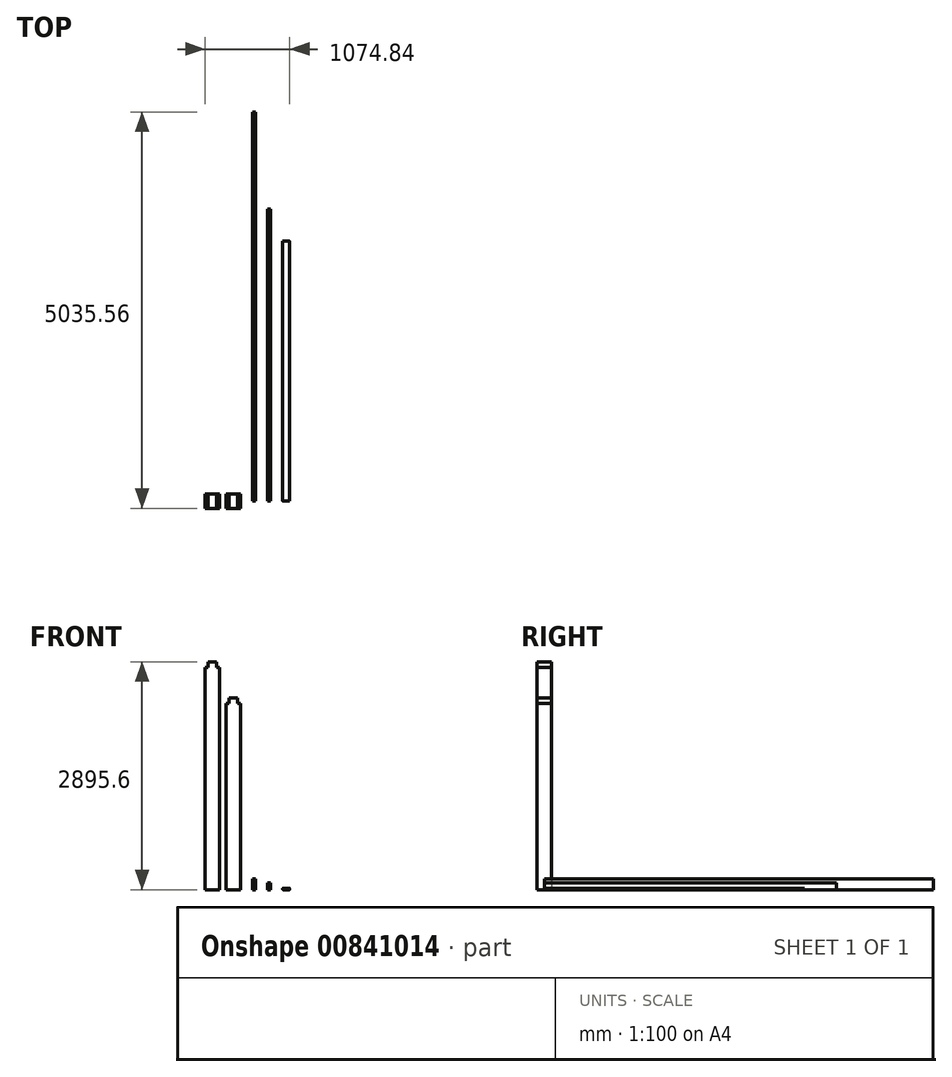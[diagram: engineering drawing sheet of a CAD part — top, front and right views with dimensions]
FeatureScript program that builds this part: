
annotation { "Feature Type Name" : "Feature", "Feature Type Description" : "" }
export const myFeature = defineFeature(function(context is Context, id is Id, definition is map)
    precondition{}
    {
        {
            var Q0;
            Q0=qCreatedBy(makeId("Top.planeOp"),FACE);
            var sketch = newSketch(context, id + "F0", { "sketchPlane" : qUnion([Q0])});
            skLineSegment(sketch, "E0.bottom", {"start": v(92.07, -92.08) * mm, "end": v(-92.08, -92.07) * mm});
            skLineSegment(sketch, "E0.top", {"start": v(92.07, 92.07) * mm, "end": v(-92.08, 92.08) * mm});
            skLineSegment(sketch, "E0.left", {"start": v(92.07, -92.08) * mm, "end": v(92.08, 92.08) * mm});
            skLineSegment(sketch, "E0.right", {"start": v(-92.08, -92.07) * mm, "end": v(-92.07, 92.07) * mm});
            skPoint(sketch, "E0.middle", {"position": v(0, 0) * mm});
            skLineSegment(sketch, "E1.bottom", {"start": v(360.46, -92.08) * mm, "end": v(176.31, -92.08) * mm});
            skLineSegment(sketch, "E1.top", {"start": v(360.46, 92.08) * mm, "end": v(176.31, 92.08) * mm});
            skLineSegment(sketch, "E1.left", {"start": v(360.46, -92.08) * mm, "end": v(360.46, 92.07) * mm});
            skLineSegment(sketch, "E1.right", {"start": v(176.31, -92.08) * mm, "end": v(176.31, 92.08) * mm});
            skPoint(sketch, "E1.middle", {"position": v(268.39, 0) * mm});
            skPoint(sketch, "E1.middle.positionSnap0", {"position": v(92.08, 0) * mm});
            skPoint(sketch, "E1.centerSnap0", {"position": v(92.08, 0) * mm});
            skSolve(sketch);
        }
        {
            var Q0;
            Q0=makeQuery(id+"F0.imprint","IMPRINT",FACE,{"disambiguationData":[TD([[makeQuery(id+"F0.imprint","IMPRINT",EDGE,{"derivedFrom":sQuery(id+"F0.wireOp",EDGE,"E0.bottom")}),-1.0]])]});
            extrude(context, id + "F1", {"entities" : qUnion([Q0]), "depth" : 2895.6 * mm, "offsetDistance" : 25.4 * mm});
        }
        {
            var Q0;
            Q0=makeQuery(id+"F0.imprint","IMPRINT",FACE,{"disambiguationData":[TD([[makeQuery(id+"F0.imprint","IMPRINT",EDGE,{"derivedFrom":sQuery(id+"F0.wireOp",EDGE,"E1.bottom")}),-1.0]])]});
            extrude(context, id + "F2", {"entities" : qUnion([Q0]), "depth" : 2438.4 * mm, "offsetDistance" : 25.4 * mm});
        }
        {
            var Q0;
            Q0=qCreatedBy(makeId("Front.planeOp"),FACE);
            var sketch = newSketch(context, id + "F3", { "sketchPlane" : qUnion([Q0])});
            skLineSegment(sketch, "E2.bottom", {"start": v(512.86, 0) * mm, "end": v(550.96, 0) * mm});
            skLineSegment(sketch, "E2.top", {"start": v(512.86, 139.7) * mm, "end": v(550.96, 139.7) * mm});
            skLineSegment(sketch, "E2.left", {"start": v(512.86, 0) * mm, "end": v(512.86, 139.7) * mm});
            skLineSegment(sketch, "E2.right", {"start": v(550.96, 0) * mm, "end": v(550.96, 139.7) * mm});
            skSolve(sketch);
        }
        {
            var Q0;
            Q0=makeQuery(id+"F3.imprint","IMPRINT",FACE,{"disambiguationData":[TD([[makeQuery(id+"F3.imprint","IMPRINT",EDGE,{"derivedFrom":sQuery(id+"F3.wireOp",EDGE,"E2.bottom")}),1.0]])]});
            extrude(context, id + "F4", {"entities" : qUnion([Q0]), "oppositeDirection" : true, "depth" : 4943.47 * mm, "offsetDistance" : 25.4 * mm});
        }
        {
            var Q0;
            Q0=makeQuery(id+"F2.opExtrude","SWEPT_FACE",FACE,{"disambiguationData":[OSD([sQuery(id+"F0.wireOp",EDGE,"E1.bottom")])]});
            var sketch = newSketch(context, id + "F5", { "sketchPlane" : qUnion([Q0])});
            skLineSegment(sketch, "E3.bottom", {"start": v(360.46, 2438.4) * mm, "end": v(322.36, 2438.4) * mm});
            skLineSegment(sketch, "E3.top", {"start": v(360.46, 2368.55) * mm, "end": v(322.36, 2368.55) * mm});
            skLineSegment(sketch, "E3.left", {"start": v(360.46, 2438.4) * mm, "end": v(360.46, 2368.55) * mm});
            skLineSegment(sketch, "E3.right", {"start": v(322.36, 2438.4) * mm, "end": v(322.36, 2368.55) * mm});
            skLineSegment(sketch, "E4", {"start": v(268.39, 2438.4) * mm, "end": v(268.39, 2178.62) * mm});
            skLineSegment(sketch, "E5.MirrorCS", {"start": v(214.41, 2438.4) * mm, "end": v(214.41, 2368.55) * mm});
            skLineSegment(sketch, "E6.MirrorCS", {"start": v(176.31, 2438.4) * mm, "end": v(214.41, 2438.4) * mm});
            skLineSegment(sketch, "E7.MirrorCS", {"start": v(176.31, 2368.55) * mm, "end": v(214.41, 2368.55) * mm});
            skLineSegment(sketch, "E8.MirrorCS", {"start": v(176.31, 2438.4) * mm, "end": v(176.31, 2368.55) * mm});
            skSolve(sketch);
        }
        {
            var Q0;
            Q0 = qSketchRegion(id + "F5", true);
            var Q1;
            Q1=makeQuery(id+"F2.opExtrude","SWEPT_FACE",FACE,{"disambiguationData":[OSD([sQuery(id+"F0.wireOp",EDGE,"E1.top")])]});
            extrude(context, id + "F6", {"entities" : qUnion([Q0]), "operationType" : NewBodyOperationType.REMOVE, "endBound" : BoundingType.UP_TO_SURFACE, "oppositeDirection" : true, "depth" : 25.4 * mm, "endBoundEntityFace" : qUnion([Q1]), "offsetDistance" : 25.4 * mm});
        }
        {
            var Q0;
            Q0=makeQuery(id+"F1.opExtrude","SWEPT_FACE",FACE,{"disambiguationData":[OSD([sQuery(id+"F0.wireOp",EDGE,"E0.bottom")])]});
            var sketch = newSketch(context, id + "F7", { "sketchPlane" : qUnion([Q0])});
            skLineSegment(sketch, "E9", {"start": v(0, 2895.6) * mm, "end": v(0, 2754.1) * mm});
            skLineSegment(sketch, "E10.bottom", {"start": v(-92.08, 2895.6) * mm, "end": v(-53.98, 2895.6) * mm});
            skLineSegment(sketch, "E10.top", {"start": v(-92.08, 2825.75) * mm, "end": v(-53.98, 2825.75) * mm});
            skLineSegment(sketch, "E10.left", {"start": v(-92.08, 2895.6) * mm, "end": v(-92.08, 2825.75) * mm});
            skLineSegment(sketch, "E10.right", {"start": v(-53.98, 2895.6) * mm, "end": v(-53.98, 2825.75) * mm});
            skLineSegment(sketch, "E11.MirrorCS", {"start": v(92.08, 2895.6) * mm, "end": v(92.08, 2825.75) * mm});
            skLineSegment(sketch, "E12.MirrorCS", {"start": v(92.08, 2825.75) * mm, "end": v(53.98, 2825.75) * mm});
            skLineSegment(sketch, "E13.MirrorCS", {"start": v(92.08, 2895.6) * mm, "end": v(53.98, 2895.6) * mm});
            skLineSegment(sketch, "E14.MirrorCS", {"start": v(53.98, 2895.6) * mm, "end": v(53.98, 2825.75) * mm});
            skSolve(sketch);
        }
        {
            var Q0;
            Q0 = qSketchRegion(id + "F7", true);
            var Q1;
            Q1=makeQuery(id+"F1.opExtrude","SWEPT_FACE",FACE,{"disambiguationData":[OSD([sQuery(id+"F0.wireOp",EDGE,"E0.top")])]});
            extrude(context, id + "F8", {"entities" : qUnion([Q0]), "operationType" : NewBodyOperationType.REMOVE, "endBound" : BoundingType.UP_TO_SURFACE, "oppositeDirection" : true, "depth" : 25.4 * mm, "endBoundEntityFace" : qUnion([Q1]), "offsetDistance" : 25.4 * mm});
        }
        {
            var Q0;
            Q0=qCreatedBy(makeId("Front.planeOp"),FACE);
            var sketch = newSketch(context, id + "F9", { "sketchPlane" : qUnion([Q0])});
            skLineSegment(sketch, "E15.bottom", {"start": v(703.36, 0) * mm, "end": v(741.46, 0) * mm});
            skLineSegment(sketch, "E15.top", {"start": v(703.36, 88.9) * mm, "end": v(741.46, 88.9) * mm});
            skLineSegment(sketch, "E15.left", {"start": v(703.36, 0) * mm, "end": v(703.36, 88.9) * mm});
            skLineSegment(sketch, "E15.right", {"start": v(741.46, 0) * mm, "end": v(741.46, 88.9) * mm});
            skSolve(sketch);
        }
        {
            var Q0;
            Q0=makeQuery(id+"F9.imprint","IMPRINT",FACE,{"disambiguationData":[TD([[makeQuery(id+"F9.imprint","IMPRINT",EDGE,{"derivedFrom":sQuery(id+"F9.wireOp",EDGE,"E15.bottom")}),1.0]])]});
            extrude(context, id + "F10", {"entities" : qUnion([Q0]), "oppositeDirection" : true, "depth" : 3708.4 * mm, "offsetDistance" : 25.4 * mm});
        }
        {
            var Q0;
            Q0=qCreatedBy(makeId("Front.planeOp"),FACE);
            var sketch = newSketch(context, id + "F11", { "sketchPlane" : qUnion([Q0])});
            skLineSegment(sketch, "E16.bottom", {"start": v(897.04, 0) * mm, "end": v(979.59, 0) * mm});
            skLineSegment(sketch, "E16.top", {"start": v(897.04, 19.05) * mm, "end": v(979.59, 19.05) * mm});
            skLineSegment(sketch, "E16.left", {"start": v(893.86, 3.17) * mm, "end": v(893.86, 15.88) * mm});
            skLineSegment(sketch, "E16.right", {"start": v(982.76, 3.18) * mm, "end": v(982.76, 15.88) * mm});
            skPoint(sketch, "E17.visualSharp", {"position": v(893.86, 19.05) * mm});
            skArc(sketch, "E17.filletArc", {"start": v(897.04, 19.05) * mm, "mid": v(894.8, 18.12) * mm, "end": v(893.86, 15.88) * mm});
            skPoint(sketch, "E18.visualSharp", {"position": v(893.86, 0) * mm});
            skArc(sketch, "E18.filletArc", {"start": v(893.86, 3.17) * mm, "mid": v(894.8, 0.93) * mm, "end": v(897.04, 0) * mm});
            skPoint(sketch, "E19.visualSharp", {"position": v(982.76, 0) * mm});
            skArc(sketch, "E19.filletArc", {"start": v(979.59, 0) * mm, "mid": v(981.83, 0.93) * mm, "end": v(982.76, 3.18) * mm});
            skPoint(sketch, "E20.visualSharp", {"position": v(982.76, 19.05) * mm});
            skArc(sketch, "E20.filletArc", {"start": v(982.76, 15.88) * mm, "mid": v(981.83, 18.12) * mm, "end": v(979.59, 19.05) * mm});
            skSolve(sketch);
        }
        {
            var Q0;
            Q0 = qSketchRegion(id + "F11", true);
            extrude(context, id + "F12", {"entities" : qUnion([Q0]), "oppositeDirection" : true, "depth" : 3302 * mm, "offsetDistance" : 25.4 * mm});
        }
    });
